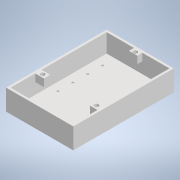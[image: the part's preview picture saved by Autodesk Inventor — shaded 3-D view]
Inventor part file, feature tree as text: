
AUTODESK INVENTOR PART (.ipt)
format: ipt  version: 2022 (Build 260153000, 153)  size: 216,576 bytes
history: native  units: mm
features: reference x12, sketch x7, extrude x6, other x4, projected_geometry x2
ambient origin geometry x8: Origin, YZ Plane, XZ Plane, XY Plane, X Axis, Y Axis, Z Axis, Center Point
bodies: Body1 (feature_tree)
feature tree (31):
  other  "Твердое тело1"
  extrude  "Выдавливание1"  Depth=200.0mm
  extrude  "Выдавливание2"  Depth=200.0mm
  extrude  "Выдавливание3"  Depth=3.0mm TaperAngle=0.0deg
  extrude  "Выдавливание4"  Depth=3.0mm TaperAngle=0.0deg
  sketch  "Эскиз5"
  extrude  "Выдавливание5"  Depth=3.0mm
  extrude  "Выдавливание6"  Depth=3.0mm
  sketch  "Эскиз1"
  sketch  "Эскиз2"
  projected_geometry  "Спроецированная петля1"
  sketch  "Эскиз3"
  projected_geometry  "Спроецированная петля2"
  sketch  "Эскиз4"
  reference  "Ссылка1"
  sketch  "Эскиз6"
  reference  "Ссылка2"
  reference  "Ссылка3"
  reference  "Ссылка4"
  sketch  "Эскиз7"
  reference  "Ссылка5"
  reference  "Ссылка6"
  reference  "Ссылка7"
  reference  "Ссылка8"
  reference  "Ссылка9"
  reference  "Ссылка10"
  reference  "Ссылка11"
  reference  "Ссылка12"
  other  "Сборка2"
  other  "Hold_18650-4:1"
  other  "goruntu modulu:1"
